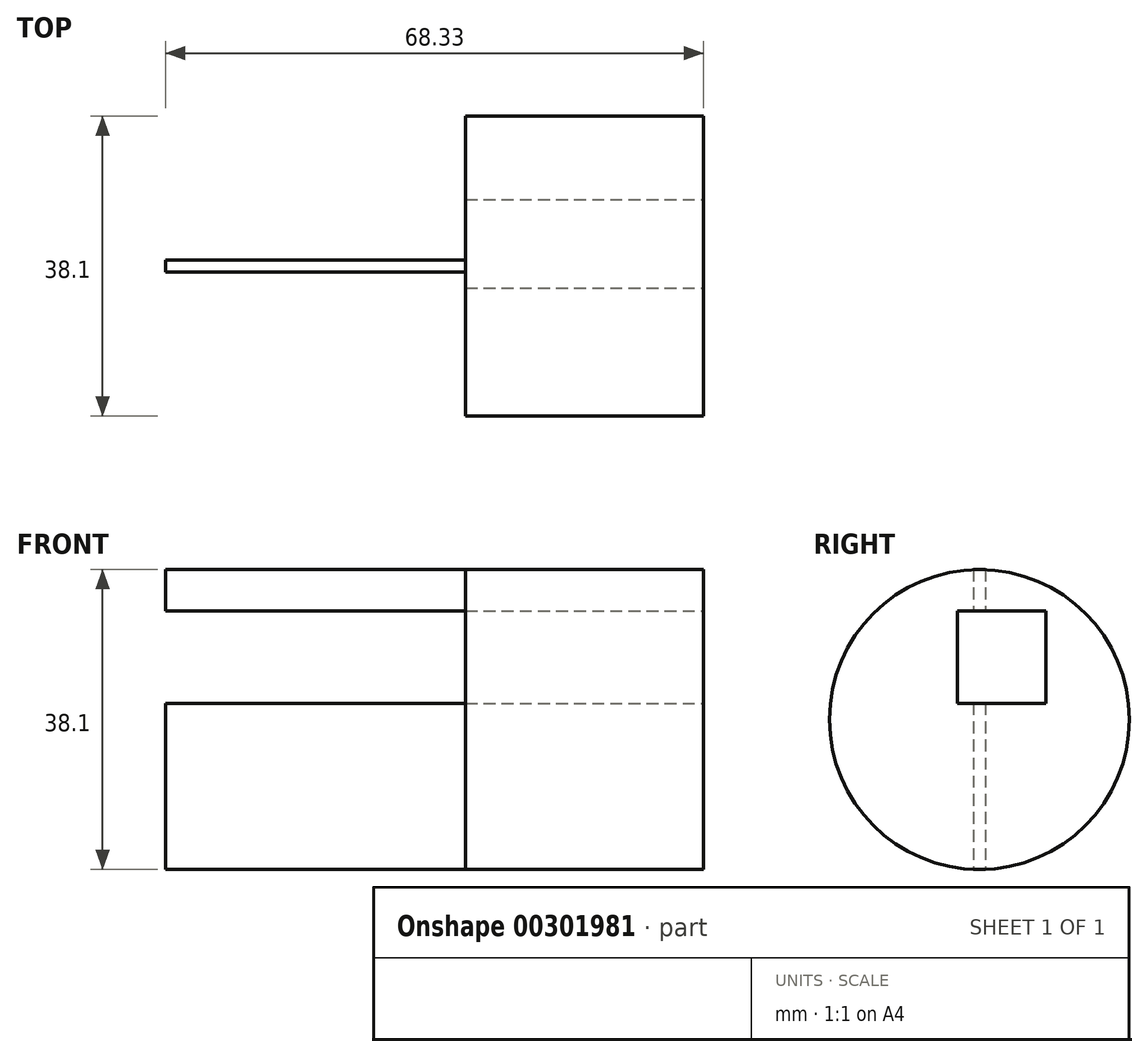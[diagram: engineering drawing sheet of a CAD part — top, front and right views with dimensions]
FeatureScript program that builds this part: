
annotation { "Feature Type Name" : "Feature", "Feature Type Description" : "" }
export const myFeature = defineFeature(function(context is Context, id is Id, definition is map)
    precondition{}
    {
        {
            assignVariable(context, id + "F0", {"name" : "cube_side", "anyValue" : 1.5});
        }
        {
            var Q0;
            Q0=qCreatedBy(makeId("Front.planeOp"),FACE);
            var sketch = newSketch(context, id + "F1", { "sketchPlane" : qUnion([Q0])});
            skLineSegment(sketch, "E0.bottom", {"start": v(-19.05, 19.05) * mm, "end": v(19.05, 19.05) * mm});
            skLineSegment(sketch, "E0.top", {"start": v(-19.05, -19.05) * mm, "end": v(19.05, -19.05) * mm});
            skLineSegment(sketch, "E0.left", {"start": v(-19.05, 19.05) * mm, "end": v(-19.05, -19.05) * mm});
            skLineSegment(sketch, "E0.right", {"start": v(19.05, 19.05) * mm, "end": v(19.05, -19.05) * mm});
            skPoint(sketch, "E0.middle", {"position": v(0, 0) * mm});
            skSolve(sketch);
        }
        {
            var Q0;
            Q0 = qSketchRegion(id + "F1", true);
            extrude(context, id + "F2", {"entities" : qUnion([Q0]), "endBound" : BoundingType.SYMMETRIC, "depth" : (getVariable(context, 'cube_side')) * mm});
        }
        {
            var Q0;
            Q0=makeQuery(id+"F2.opExtrude","SWEPT_FACE",FACE,{"disambiguationData":[OSD([sQuery(id+"F1.wireOp",EDGE,"E0.right")])]});
            var sketch = newSketch(context, id + "F3", { "sketchPlane" : qUnion([Q0])});
            skCircle(sketch, "E1", {"center": v(0, 0) * mm, "radius": 19.05 * mm});
            skSolve(sketch);
        }
        {
            var Q0;
            Q0 = qSketchRegion(id + "F3", true);
            extrude(context, id + "F4", {"entities" : qUnion([Q0]), "operationType" : NewBodyOperationType.ADD, "depth" : 30.23 * mm});
        }
        {
            var Q0;
            Q0=makeQuery(id+"F4.opExtrude","CAP_FACE",FACE,{"disambiguationData":[OSD([sQuery(id+"F3.wireOp",EDGE,"E1")])],"isStart":false});
            var sketch = newSketch(context, id + "F5", { "sketchPlane" : qUnion([Q0])});
            skLineSegment(sketch, "E2.bottom", {"start": v(8.44, 2.04) * mm, "end": v(-2.81, 2.04) * mm});
            skLineSegment(sketch, "E2.top", {"start": v(8.44, 13.8) * mm, "end": v(-2.81, 13.8) * mm});
            skLineSegment(sketch, "E2.left", {"start": v(8.44, 2.04) * mm, "end": v(8.44, 13.8) * mm});
            skLineSegment(sketch, "E2.right", {"start": v(-2.81, 2.04) * mm, "end": v(-2.81, 13.8) * mm});
            skPoint(sketch, "E2.middle", {"position": v(2.81, 7.92) * mm});
            skSolve(sketch);
        }
        {
            var Q0;
            Q0 = qSketchRegion(id + "F5", true);
            extrude(context, id + "F6", {"entities" : qUnion([Q0]), "operationType" : NewBodyOperationType.REMOVE, "endBound" : BoundingType.THROUGH_ALL, "oppositeDirection" : true, "depth" : 25.4 * mm});
        }
    });
